# Revit family: Ceiling_Sensor-Dual-Hubbell_Wiring-ATD
name_source: partatom
category: Lighting Devices
revit_build: Autodesk Revit 2015 (Build: 20140606_1530(x64)
units: mm (PartAtom-declared; Revit-internal decimal feet)

## types (3) — shared parameters
Ambient Light = 1 to 1000 foot candles
Apparent Load = 0.000 VA
Connector Description 1 = Power Supply
Connector Description 2 = Controls
Default Elevation = 48 "
Description = Dual Technology Occupancy Sensors combine both Passive Infrared (PIR) 
and Ultrasonic (US) technologies for maximum reliability.
Device Material = Plastic - Hubbell - White
Glass = Plastic - Hubbell - Polyethylene
Load Classification = Other
Manufacturer = Hubbell Wiring Device-Kellems
Number of Poles = 1
Operating Temperature = 32°F to 104°F (0°C to 40°C) with rate of change not
exceeding 20°F (11°C) per hour
Power Factor = 1
Product Documentation Link = http://ecatalog.hubbell-wiring.com
Product Page URL = http://ecatalog.hubbell-wiring.com
Product data url = https://bimobject.com
Sensitivity = Adaptive 0 to 100%
Storage Temperature = -20°F to 150°F (-29°C to 65°C); 0% to 95%
non-condensing relative humidity
Time Delay = Test (8 seconds), adaptive 8 to 40 minutes
URL = http://www.hubbell-wiring.com
Voltage = 24 V

## per-type parameters (varying)
| type | Coverage | Coverage Area | Sensors Option |
| ATD2000C | 360.00° | Field of View : 2000 sq.ft. | ATD2000 |
| ATD1000C | 180.00° | Field of View : 1000 sq.ft. | ATD1000C-500C |
| ATD500C | 180.00° | Field of View : 500 sq.ft. | ATD1000C-500C |

note: column(s) folded — value = type name in every type: Model

## geometry (parser evidence)
native form markers: Sweep x10
no freeform markers — native parametric forms only
